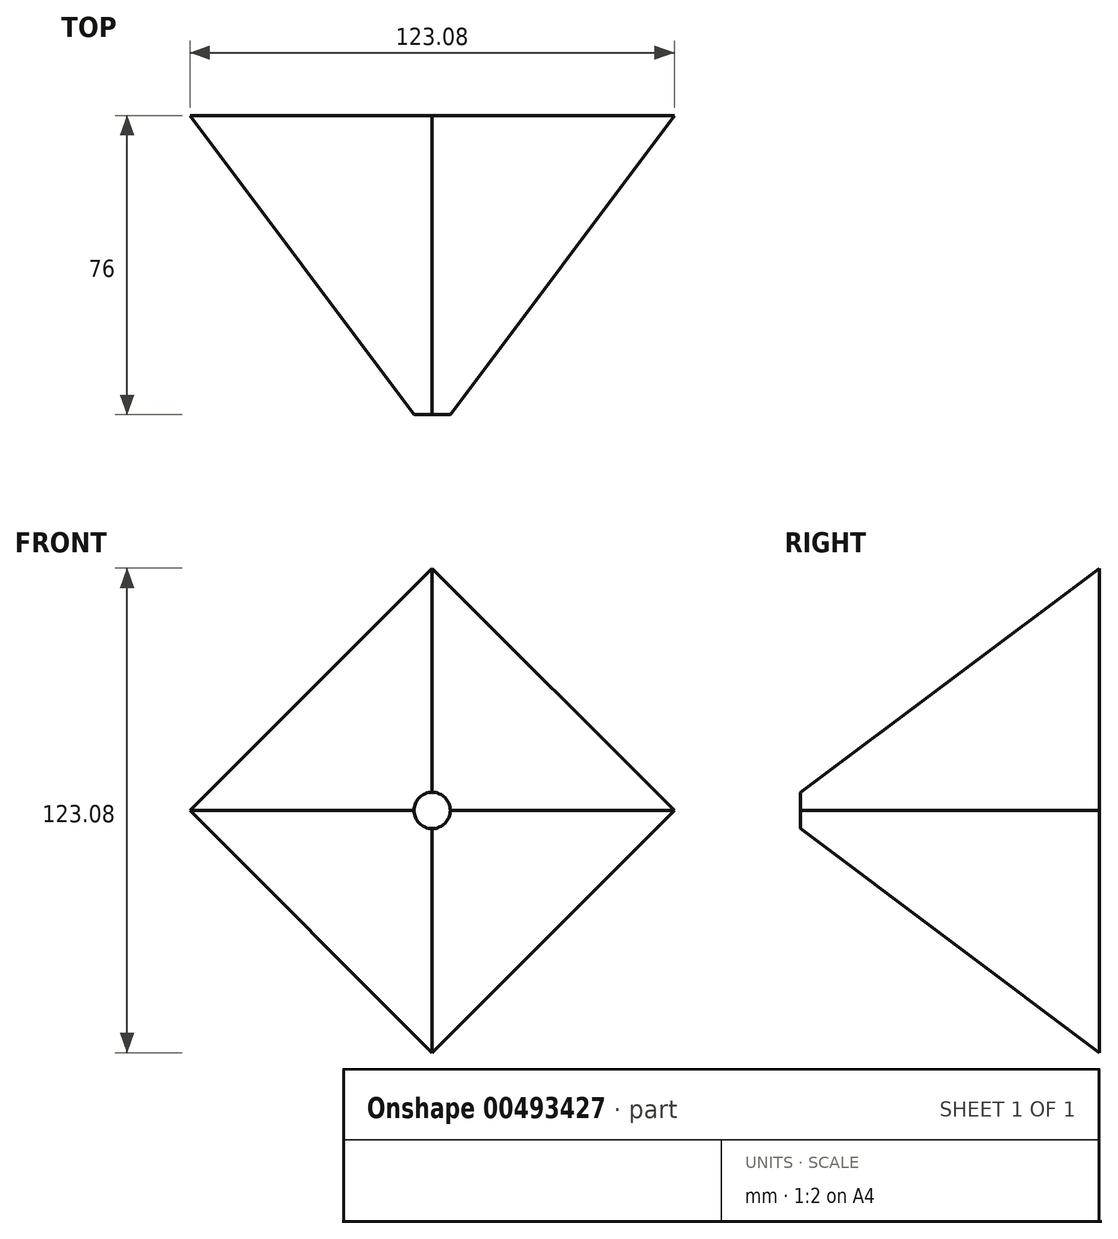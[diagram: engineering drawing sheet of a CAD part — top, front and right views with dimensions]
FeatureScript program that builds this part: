
annotation { "Feature Type Name" : "Feature", "Feature Type Description" : "" }
export const myFeature = defineFeature(function(context is Context, id is Id, definition is map)
    precondition{}
    {
        {
            var Q0;
            Q0=qCreatedBy(makeId("Front.planeOp"),FACE);
            var sketch = newSketch(context, id + "F0", { "sketchPlane" : qUnion([Q0])});
            skCircle(sketch, "E0.cCircle", {"center": v(0, 0) * mm, "radius": 61.54 * mm, "construction": true});
            skLineSegment(sketch, "E0.0", {"start": v(0, 61.54) * mm, "end": v(61.54, 0) * mm});
            skLineSegment(sketch, "E0.1", {"start": v(61.54, 0) * mm, "end": v(0, -61.54) * mm});
            skLineSegment(sketch, "E0.2", {"start": v(0, -61.54) * mm, "end": v(-61.54, 0) * mm});
            skLineSegment(sketch, "E0.3", {"start": v(-61.54, 0) * mm, "end": v(0, 61.54) * mm});
            skSolve(sketch);
        }
        {
            var Q0;
            Q0=qCreatedBy(makeId("Front.planeOp"),FACE);
            cPlane(context, id + "F1", {"entities" : qUnion([Q0]), "cplaneType" : CPlaneType.OFFSET, "offset" : 76 * mm, "width" : 150 * mm, "height" : 150 * mm});
        }
        {
            var Q0;
            Q0=qCreatedBy(id+"F1.planeOp",FACE);
            var sketch = newSketch(context, id + "F2", { "sketchPlane" : qUnion([Q0])});
            skCircle(sketch, "E1", {"center": v(0, 0) * mm, "radius": 4.61 * mm});
            skSolve(sketch);
        }
        {
            var Q0;
            Q0=makeQuery(id+"F2.imprint","IMPRINT",FACE,{"disambiguationData":[TD([[makeQuery(id+"F2.imprint","IMPRINT",EDGE,{"derivedFrom":sQuery(id+"F2.wireOp",EDGE,"E1")}),1.0]])]});
            var Q1;
            Q1=makeQuery(id+"F0.imprint","IMPRINT",FACE,{"disambiguationData":[TD([[makeQuery(id+"F0.imprint","IMPRINT",EDGE,{"derivedFrom":sQuery(id+"F0.wireOp",EDGE,"E0.0")}),-1.0]])]});
            loft(context, id + "F3", {"sheetProfilesArray" : [{ "sheetProfileEntities" : qUnion([Q0]) }, { "sheetProfileEntities" : qUnion([Q1]) }]});
        }
    });
